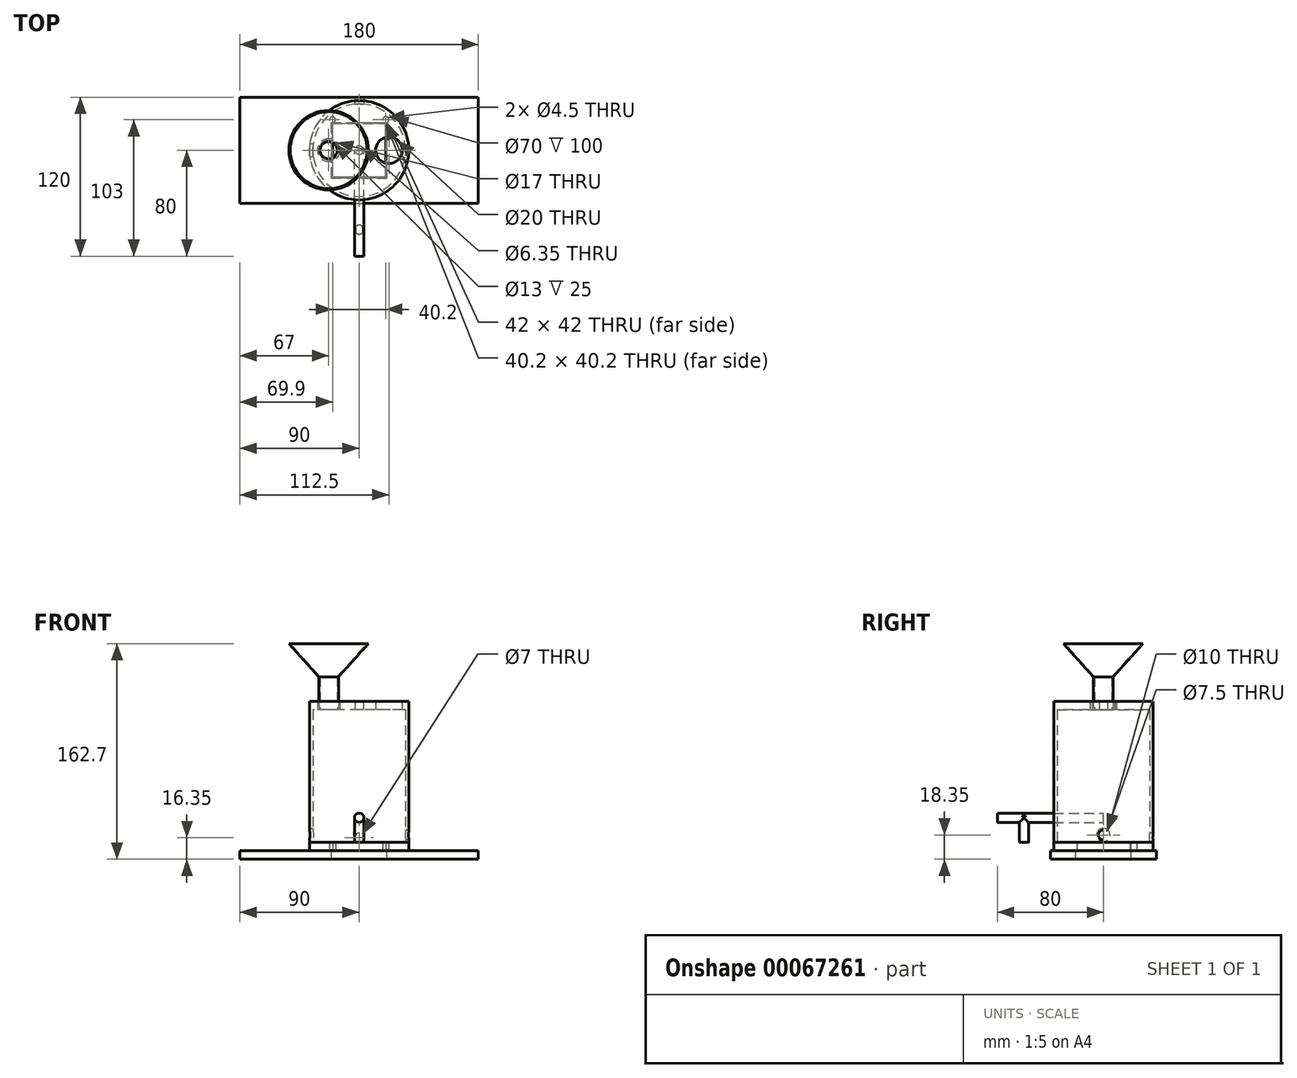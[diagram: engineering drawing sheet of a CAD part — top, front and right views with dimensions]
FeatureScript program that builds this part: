
annotation { "Feature Type Name" : "Feature", "Feature Type Description" : "" }
export const myFeature = defineFeature(function(context is Context, id is Id, definition is map)
    precondition{}
    {
        {
            var Q0;
            Q0=qCreatedBy(makeId("Top.planeOp"),FACE);
            var sketch = newSketch(context, id + "F0", { "sketchPlane" : qUnion([Q0])});
            skCircle(sketch, "E0", {"center": v(0, 0) * mm, "radius": 37.5 * mm});
            skLineSegment(sketch, "E1.bottom", {"start": v(-20.1, -20.1) * mm, "end": v(20.1, -20.1) * mm});
            skLineSegment(sketch, "E1.top", {"start": v(-20.1, 20.1) * mm, "end": v(20.1, 20.1) * mm});
            skLineSegment(sketch, "E1.left", {"start": v(-20.1, -20.1) * mm, "end": v(-20.1, 20.1) * mm});
            skLineSegment(sketch, "E1.right", {"start": v(20.1, -20.1) * mm, "end": v(20.1, 20.1) * mm});
            skPoint(sketch, "E2", {"position": v(0, -20.1) * mm});
            skPoint(sketch, "E3", {"position": v(-20.1, 0) * mm});
            skCircle(sketch, "E4", {"center": v(-20.1, 23) * mm, "radius": 2.25 * mm});
            skCircle(sketch, "E5", {"center": v(20.1, 23) * mm, "radius": 2.25 * mm});
            skSolve(sketch);
        }
        {
            var Q0;
            Q0=makeQuery(id+"F0.imprint","IMPRINT",FACE,{"disambiguationData":[TD([[makeQuery(id+"F0.imprint","IMPRINT",EDGE,{"derivedFrom":sQuery(id+"F0.wireOp",EDGE,"E0")}),1.0]])]});
            extrude(context, id + "F1", {"entities" : qUnion([Q0]), "depth" : 6.35 * mm});
        }
        {
            var Q0;
            Q0=qCreatedBy(makeId("Top.planeOp"),FACE);
            cPlane(context, id + "F2", {"entities" : qUnion([Q0]), "cplaneType" : CPlaneType.OFFSET, "offset" : 6.35 * mm, "width" : 150 * mm, "height" : 150 * mm});
        }
        {
            var Q0;
            Q0=qCreatedBy(id+"F2.planeOp",FACE);
            var sketch = newSketch(context, id + "F3", { "sketchPlane" : qUnion([Q0])});
            skCircle(sketch, "E6", {"center": v(0, 0) * mm, "radius": 37.5 * mm});
            skCircle(sketch, "E7", {"center": v(0, 0) * mm, "radius": 35 * mm});
            skSolve(sketch);
        }
        {
            var Q0;
            Q0 = qSketchRegion(id + "F3", true);
            extrude(context, id + "F4", {"entities" : qUnion([Q0]), "depth" : 100 * mm});
        }
        {
            var Q0;
            Q0=qCreatedBy(id+"F2.planeOp",FACE);
            cPlane(context, id + "F5", {"entities" : qUnion([Q0]), "cplaneType" : CPlaneType.OFFSET, "offset" : 100 * mm, "width" : 150 * mm, "height" : 150 * mm});
        }
        {
            var Q0;
            Q0=qCreatedBy(id+"F5.planeOp",FACE);
            var sketch = newSketch(context, id + "F6", { "sketchPlane" : qUnion([Q0])});
            skCircle(sketch, "E8", {"center": v(0, 0) * mm, "radius": 37.5 * mm});
            skCircle(sketch, "E9", {"center": v(-23, 0) * mm, "radius": 8.5 * mm});
            skCircle(sketch, "E10", {"center": v(22.5, 0) * mm, "radius": 10 * mm});
            skCircle(sketch, "E11", {"center": v(0, 0) * mm, "radius": 3.18 * mm});
            skSolve(sketch);
        }
        {
            var Q0;
            Q0 = qSketchRegion(id + "F6", true);
            extrude(context, id + "F7", {"entities" : qUnion([Q0]), "operationType" : NewBodyOperationType.ADD, "depth" : 6.35 * mm});
        }
        {
            var Q0;
            Q0=qCreatedBy(id+"F5.planeOp",FACE);
            cPlane(context, id + "F8", {"entities" : qUnion([Q0]), "cplaneType" : CPlaneType.OFFSET, "offset" : 50 * mm, "width" : 150 * mm, "height" : 150 * mm});
        }
        {
            var Q0;
            Q0=qCreatedBy(makeId("Top.planeOp"),FACE);
            var sketch = newSketch(context, id + "F9", { "sketchPlane" : qUnion([Q0])});
            skLineSegment(sketch, "E12.bottom", {"start": v(-90, -40) * mm, "end": v(90, -40) * mm});
            skLineSegment(sketch, "E12.top", {"start": v(-90, 40) * mm, "end": v(90, 40) * mm});
            skLineSegment(sketch, "E12.left", {"start": v(-90, -40) * mm, "end": v(-90, 40) * mm});
            skLineSegment(sketch, "E12.right", {"start": v(90, -40) * mm, "end": v(90, 40) * mm});
            skPoint(sketch, "E13", {"position": v(0, -40) * mm});
            skPoint(sketch, "E14", {"position": v(-90, 0) * mm});
            skLineSegment(sketch, "E15.bottom", {"start": v(-21, -21) * mm, "end": v(21, -21) * mm});
            skLineSegment(sketch, "E15.top", {"start": v(-21, 21) * mm, "end": v(21, 21) * mm});
            skLineSegment(sketch, "E15.left", {"start": v(-21, -21) * mm, "end": v(-21, 21) * mm});
            skLineSegment(sketch, "E15.right", {"start": v(21, -21) * mm, "end": v(21, 21) * mm});
            skPoint(sketch, "E16", {"position": v(0, -21) * mm});
            skPoint(sketch, "E17", {"position": v(-21, 0) * mm});
            skPoint(sketch, "E18", {"position": v(-86.83, 0) * mm});
            skPoint(sketch, "E19", {"position": v(0, 36.83) * mm});
            skPoint(sketch, "E19.positionSnap0", {"position": v(0, 21) * mm});
            skSolve(sketch);
        }
        {
            var Q0;
            Q0 = qSketchRegion(id + "F9", true);
            extrude(context, id + "F10", {"entities" : qUnion([Q0]), "oppositeDirection" : true, "depth" : 6.35 * mm});
        }
        {
            var Q0;
            Q0=qCreatedBy(makeId("Right.planeOp"),FACE);
            var sketch = newSketch(context, id + "F11", { "sketchPlane" : qUnion([Q0])});
            skCircle(sketch, "E20", {"center": v(0, 12) * mm, "radius": 5 * mm});
            skSolve(sketch);
        }
        {
            var Q0;
            Q0 = qSketchRegion(id + "F11", true);
            var Q1;
            Q1 = qSketchRegion(id + "F13", true);
            extrude(context, id + "F12", {"entities" : qUnion([Q0, Q1]), "operationType" : NewBodyOperationType.REMOVE, "oppositeDirection" : true, "depth" : 77 * mm});
        }
        {
            var Q0;
            Q0=qCreatedBy(makeId("Right.planeOp"),FACE);
            var sketch = newSketch(context, id + "F13", { "sketchPlane" : qUnion([Q0])});
            skCircle(sketch, "E21", {"center": v(0, 12) * mm, "radius": 3.75 * mm});
            skSolve(sketch);
        }
        {
            var Q0;
            Q0 = qSketchRegion(id + "F13", true);
            extrude(context, id + "F14", {"entities" : qUnion([Q0]), "operationType" : NewBodyOperationType.REMOVE, "depth" : 75 * mm});
        }
        {
            var Q0;
            Q0=qCreatedBy(makeId("Front.planeOp"),FACE);
            var sketch = newSketch(context, id + "F15", { "sketchPlane" : qUnion([Q0])});
            skCircle(sketch, "E22", {"center": v(0, 25) * mm, "radius": 3.5 * mm});
            skSolve(sketch);
        }
        {
            var Q0;
            Q0 = qSketchRegion(id + "F15", true);
            extrude(context, id + "F16", {"entities" : qUnion([Q0]), "depth" : 80 * mm});
        }
        {
            var Q0;
            Q0=qCreatedBy(id+"F2.planeOp",FACE);
            var sketch = newSketch(context, id + "F17", { "sketchPlane" : qUnion([Q0])});
            skCircle(sketch, "E23", {"center": v(0, -60) * mm, "radius": 3.5 * mm});
            skSolve(sketch);
        }
        {
            var Q0;
            Q0 = qSketchRegion(id + "F17", true);
            extrude(context, id + "F18", {"entities" : qUnion([Q0]), "operationType" : NewBodyOperationType.ADD, "depth" : 20 * mm});
        }
        {
            var Q0;
            Q0=qCreatedBy(makeId("Front.planeOp"),FACE);
            var sketch = newSketch(context, id + "F19", { "sketchPlane" : qUnion([Q0])});
            skCircle(sketch, "E24", {"center": v(0, 10) * mm, "radius": 3.5 * mm});
            skSolve(sketch);
        }
        {
            var Q0;
            Q0 = qSketchRegion(id + "F19", true);
            extrude(context, id + "F20", {"entities" : qUnion([Q0]), "operationType" : NewBodyOperationType.REMOVE, "oppositeDirection" : true, "depth" : 40 * mm});
        }
        {
            var Q0;
            Q0=qCreatedBy(id+"F5.planeOp",FACE);
            var sketch = newSketch(context, id + "F21", { "sketchPlane" : qUnion([Q0])});
            skCircle(sketch, "E25", {"center": v(-23, 0) * mm, "radius": 7.5 * mm});
            skSolve(sketch);
        }
        {
            var Q0;
            Q0 = qSketchRegion(id + "F21", true);
            extrude(context, id + "F22", {"entities" : qUnion([Q0]), "depth" : 25 * mm});
        }
        {
            var Q0;
            Q0=qCreatedBy(id+"F8.planeOp",FACE);
            var sketch = newSketch(context, id + "F23", { "sketchPlane" : qUnion([Q0])});
            skCircle(sketch, "E26", {"center": v(-23, 0) * mm, "radius": 30 * mm});
            skSolve(sketch);
        }
        {
            var Q1;
            Q1=makeQuery(id+"F22.opExtrude","CAP_FACE",FACE,{"disambiguationData":[OSD([sQuery(id+"F21.wireOp",EDGE,"E25")])],"isStart":false});
            var Q2;
            Q2=makeQuery(id+"F23.imprint","IMPRINT",FACE,{"disambiguationData":[TD([[makeQuery(id+"F23.imprint","IMPRINT",EDGE,{"derivedFrom":sQuery(id+"F23.wireOp",EDGE,"E26")}),1.0]])]});
            loft(context, id + "F24", {"operationType" : NewBodyOperationType.ADD, "sheetProfilesArray" : [{ "sheetProfileEntities" : qUnion([Q1]) }, { "sheetProfileEntities" : qUnion([Q2]) }]});
        }
        {
            var Q0;
            Q0=qCreatedBy(id+"F5.planeOp",FACE);
            var sketch = newSketch(context, id + "F25", { "sketchPlane" : qUnion([Q0])});
            skCircle(sketch, "E27", {"center": v(-23, 0) * mm, "radius": 6.5 * mm});
            skSolve(sketch);
        }
        {
            var Q0;
            Q0 = qSketchRegion(id + "F25", true);
            extrude(context, id + "F26", {"entities" : qUnion([Q0]), "operationType" : NewBodyOperationType.REMOVE, "depth" : 25 * mm});
        }
        {
            var Q0;
            Q0=qCreatedBy(id+"F8.planeOp",FACE);
            var sketch = newSketch(context, id + "F27", { "sketchPlane" : qUnion([Q0])});
            skCircle(sketch, "E28", {"center": v(-23, 0) * mm, "radius": 29 * mm});
            skSolve(sketch);
        }
        {
            var Q0;
            Q0=qCreatedBy(id+"F5.planeOp",FACE);
            cPlane(context, id + "F28", {"entities" : qUnion([Q0]), "cplaneType" : CPlaneType.OFFSET, "offset" : 25 * mm, "width" : 150 * mm, "height" : 150 * mm});
        }
        {
            var Q0;
            Q0=qCreatedBy(id+"F28.planeOp",FACE);
            var sketch = newSketch(context, id + "F29", { "sketchPlane" : qUnion([Q0])});
            skCircle(sketch, "E29", {"center": v(-23, 0) * mm, "radius": 6.5 * mm});
            skSolve(sketch);
        }
        {
            var Q1;
            Q1 = qSketchRegion(id + "F27", true);
            var Q2;
            Q2 = qSketchRegion(id + "F29", true);
            loft(context, id + "F30", {"operationType" : NewBodyOperationType.REMOVE, "sheetProfilesArray" : [{ "sheetProfileEntities" : qUnion([Q1]) }, { "sheetProfileEntities" : qUnion([Q2]) }]});
        }
    });
